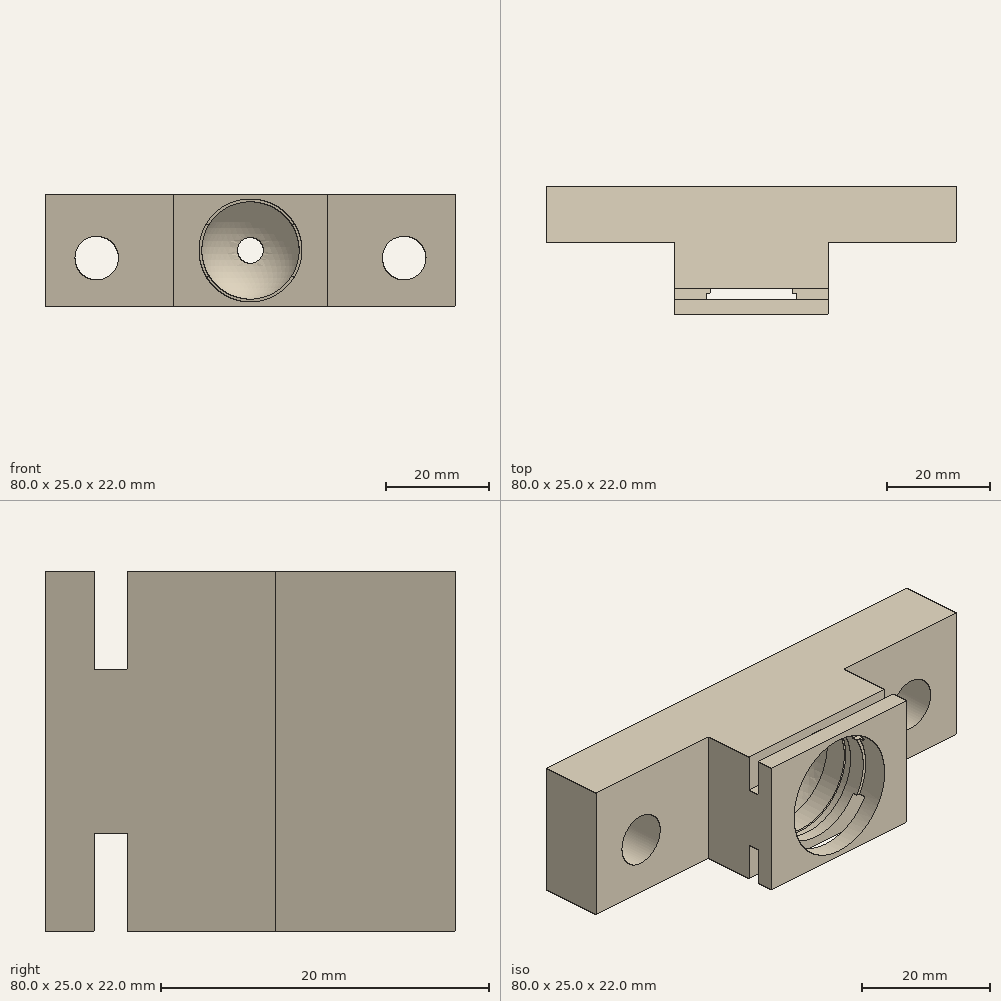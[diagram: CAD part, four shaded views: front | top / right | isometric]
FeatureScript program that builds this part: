
annotation { "Feature Type Name" : "Feature", "Feature Type Description" : "" }
export const myFeature = defineFeature(function(context is Context, id is Id, definition is map)
    precondition{}
    {
        {
            var Q0;
            Q0=qCreatedBy(makeId("Front.planeOp"),FACE);
            var sketch = newSketch(context, id + "F0", { "sketchPlane" : qUnion([Q0])});
            skLineSegment(sketch, "E0.bottom", {"start": v(40, 11) * mm, "end": v(-40, 11) * mm});
            skLineSegment(sketch, "E0.top", {"start": v(40, -11) * mm, "end": v(-40, -11) * mm});
            skLineSegment(sketch, "E0.left", {"start": v(40, 11) * mm, "end": v(40, -11) * mm});
            skLineSegment(sketch, "E0.right", {"start": v(-40, 11) * mm, "end": v(-40, -11) * mm});
            skPoint(sketch, "E0.middle", {"position": v(0, 0) * mm});
            skSolve(sketch);
        }
        {
            var Q0;
            Q0 = qSketchRegion(id + "F0", true);
            extrude(context, id + "F1", {"entities" : qUnion([Q0]), "depth" : 11 * mm, "offsetDistance" : 25 * mm});
        }
        {
            var Q0;
            Q0=makeQuery(id+"F1.opExtrude","CAP_FACE",FACE,{"disambiguationData":[OSD([sQuery(id+"F0.wireOp",EDGE,"E0.bottom"),sQuery(id+"F0.wireOp",EDGE,"E0.top"),sQuery(id+"F0.wireOp",EDGE,"E0.left"),sQuery(id+"F0.wireOp",EDGE,"E0.right")])],"isStart":false});
            var sketch = newSketch(context, id + "F2", { "sketchPlane" : qUnion([Q0])});
            skLineSegment(sketch, "E1.bottom", {"start": v(15, 11) * mm, "end": v(-15, 11) * mm});
            skLineSegment(sketch, "E1.top", {"start": v(15, -11) * mm, "end": v(-15, -11) * mm});
            skLineSegment(sketch, "E1.left", {"start": v(15, 11) * mm, "end": v(15, -11) * mm});
            skLineSegment(sketch, "E1.right", {"start": v(-15, 11) * mm, "end": v(-15, -11) * mm});
            skPoint(sketch, "E1.middle", {"position": v(0, 0) * mm});
            skSolve(sketch);
        }
        {
            var Q0;
            Q0 = qSketchRegion(id + "F2", true);
            extrude(context, id + "F3", {"entities" : qUnion([Q0]), "operationType" : NewBodyOperationType.ADD, "depth" : 14 * mm, "offsetDistance" : 25 * mm});
        }
        {
            var Q0;
            Q0=makeQuery(id+"F1.opExtrude","CAP_FACE",FACE,{"disambiguationData":[OSD([sQuery(id+"F0.wireOp",EDGE,"E0.bottom"),sQuery(id+"F0.wireOp",EDGE,"E0.top"),sQuery(id+"F0.wireOp",EDGE,"E0.left"),sQuery(id+"F0.wireOp",EDGE,"E0.right")])],"isStart":true});
            var sketch = newSketch(context, id + "F4", { "sketchPlane" : qUnion([Q0])});
            skCircle(sketch, "E2", {"center": v(30, -1.5) * mm, "radius": 4.25 * mm});
            skCircle(sketch, "E3.MirrorC", {"center": v(-30, -1.5) * mm, "radius": 4.25 * mm});
            skSolve(sketch);
        }
        {
            var Q0;
            Q0 = qSketchRegion(id + "F4", true);
            extrude(context, id + "F5", {"entities" : qUnion([Q0]), "operationType" : NewBodyOperationType.REMOVE, "endBound" : BoundingType.UP_TO_NEXT, "oppositeDirection" : true, "depth" : 25 * mm, "offsetDistance" : 25 * mm});
        }
        {
            var Q0;
            Q0=makeQuery(id+"F3.opExtrude","SWEPT_FACE",FACE,{"disambiguationData":[OSD([sQuery(id+"F2.wireOp",EDGE,"E1.right")])]});
            var sketch = newSketch(context, id + "F6", { "sketchPlane" : qUnion([Q0])});
            skLineSegment(sketch, "E4", {"start": v(22, 11) * mm, "end": v(22, 5) * mm});
            skLineSegment(sketch, "E5", {"start": v(22, 5) * mm, "end": v(20, 5) * mm});
            skLineSegment(sketch, "E6", {"start": v(20, 5) * mm, "end": v(20, 11) * mm});
            skLineSegment(sketch, "E7.MirrorCS", {"start": v(22, -11) * mm, "end": v(22, -5) * mm});
            skLineSegment(sketch, "E8.MirrorCS", {"start": v(22, -5) * mm, "end": v(20, -5) * mm});
            skLineSegment(sketch, "E9.MirrorCS", {"start": v(20, -5) * mm, "end": v(20, -11) * mm});
            skLineSegment(sketch, "E10", {"start": v(22, 11) * mm, "end": v(20, 11) * mm});
            skLineSegment(sketch, "E11", {"start": v(22, -11) * mm, "end": v(20, -11) * mm});
            skSolve(sketch);
        }
        {
            var Q0;
            Q0 = qSketchRegion(id + "F6", true);
            extrude(context, id + "F7", {"entities" : qUnion([Q0]), "operationType" : NewBodyOperationType.REMOVE, "endBound" : BoundingType.UP_TO_NEXT, "oppositeDirection" : true, "depth" : 25 * mm, "offsetDistance" : 25 * mm});
        }
        {
            var Q0;
            Q0=makeQuery(id+"F3.opExtrude","CAP_FACE",FACE,{"disambiguationData":[OSD([sQuery(id+"F2.wireOp",EDGE,"E1.bottom"),sQuery(id+"F2.wireOp",EDGE,"E1.top"),sQuery(id+"F2.wireOp",EDGE,"E1.left"),sQuery(id+"F2.wireOp",EDGE,"E1.right")])],"isStart":false});
            var sketch = newSketch(context, id + "F8", { "sketchPlane" : qUnion([Q0])});
            skCircle(sketch, "E12", {"center": v(0, 0) * mm, "radius": 10.05 * mm});
            skSolve(sketch);
        }
        {
            var Q0;
            Q0 = qSketchRegion(id + "F8", true);
            extrude(context, id + "F9", {"entities" : qUnion([Q0]), "operationType" : NewBodyOperationType.REMOVE, "oppositeDirection" : true, "depth" : 4.2 * mm, "offsetDistance" : 25 * mm});
        }
        {
            var Q0;
            Q0=makeQuery(id+"F3.opExtrude","CAP_FACE",FACE,{"disambiguationData":[OSD([sQuery(id+"F2.wireOp",EDGE,"E1.bottom"),sQuery(id+"F2.wireOp",EDGE,"E1.top"),sQuery(id+"F2.wireOp",EDGE,"E1.left"),sQuery(id+"F2.wireOp",EDGE,"E1.right")])],"isStart":false});
            var sketch = newSketch(context, id + "F10", { "sketchPlane" : qUnion([Q0])});
            skCircle(sketch, "E13", {"center": v(0, 0) * mm, "radius": 9.5 * mm});
            skSolve(sketch);
        }
        {
            var Q0;
            Q0 = qSketchRegion(id + "F10", true);
            extrude(context, id + "F11", {"entities" : qUnion([Q0]), "operationType" : NewBodyOperationType.REMOVE, "oppositeDirection" : true, "depth" : 7 * mm, "offsetDistance" : 25 * mm});
        }
        {
            var Q0;
            Q0=makeQuery(id+"F3.opExtrude","CAP_FACE",FACE,{"disambiguationData":[OSD([sQuery(id+"F2.wireOp",EDGE,"E1.bottom"),sQuery(id+"F2.wireOp",EDGE,"E1.top"),sQuery(id+"F2.wireOp",EDGE,"E1.left"),sQuery(id+"F2.wireOp",EDGE,"E1.right")])],"isStart":false});
            var sketch = newSketch(context, id + "F12", { "sketchPlane" : qUnion([Q0])});
            skCircle(sketch, "E14", {"center": v(0, 0) * mm, "radius": 9.8 * mm});
            skSolve(sketch);
        }
        {
            var Q0;
            Q0=makeQuery(id+"F12.imprint","IMPRINT",FACE,{"disambiguationData":[TD([[makeQuery(id+"F12.imprint","IMPRINT",EDGE,{"derivedFrom":sQuery(id+"F12.wireOp",EDGE,"E14")}),-1.0]])]});
            cPlane(context, id + "F13", {"entities" : qUnion([Q0]), "cplaneType" : CPlaneType.OFFSET, "offset" : 7 * mm, "oppositeDirection" : true, "width" : 150 * mm, "height" : 150 * mm});
        }
        {
            var Q0;
            Q0=qCreatedBy(id+"F13.planeOp",FACE);
            var sketch = newSketch(context, id + "F14", { "sketchPlane" : qUnion([Q0])});
            skCircle(sketch, "E15", {"center": v(0, 0) * mm, "radius": 9.8 * mm});
            skSolve(sketch);
        }
        {
            var Q0;
            Q0 = qSketchRegion(id + "F14", true);
            extrude(context, id + "F15", {"entities" : qUnion([Q0]), "operationType" : NewBodyOperationType.REMOVE, "oppositeDirection" : true, "depth" : 1.4 * mm, "offsetDistance" : 25 * mm});
        }
        {
            var Q0;
            Q0=makeQuery(id+"F12.imprint","IMPRINT",FACE,{"disambiguationData":[TD([[makeQuery(id+"F12.imprint","IMPRINT",EDGE,{"derivedFrom":sQuery(id+"F12.wireOp",EDGE,"E14")}),-1.0]])]});
            cPlane(context, id + "F16", {"entities" : qUnion([Q0]), "cplaneType" : CPlaneType.OFFSET, "offset" : 8.4 * mm, "oppositeDirection" : true, "width" : 150 * mm, "height" : 150 * mm});
        }
        {
            var Q0;
            Q0=qCreatedBy(id+"F16.planeOp",FACE);
            var sketch = newSketch(context, id + "F17", { "sketchPlane" : qUnion([Q0])});
            skCircle(sketch, "E16", {"center": v(0, 0) * mm, "radius": 9.5 * mm});
            skSolve(sketch);
        }
        {
            var Q0;
            Q0 = qSketchRegion(id + "F17", true);
            extrude(context, id + "F18", {"entities" : qUnion([Q0]), "operationType" : NewBodyOperationType.REMOVE, "oppositeDirection" : true, "depth" : 3.8 * mm, "offsetDistance" : 25 * mm});
        }
        {
            var Q0;
            Q0=makeQuery(id+"F1.opExtrude","CAP_FACE",FACE,{"disambiguationData":[OSD([sQuery(id+"F0.wireOp",EDGE,"E0.bottom"),sQuery(id+"F0.wireOp",EDGE,"E0.top"),sQuery(id+"F0.wireOp",EDGE,"E0.left"),sQuery(id+"F0.wireOp",EDGE,"E0.right")])],"isStart":true});
            var sketch = newSketch(context, id + "F19", { "sketchPlane" : qUnion([Q0])});
            skCircle(sketch, "E17", {"center": v(0, 0) * mm, "radius": 2.5 * mm});
            skSolve(sketch);
        }
        {
            var Q0;
            Q0=qCreatedBy(id+"F16.planeOp",FACE);
            var sketch = newSketch(context, id + "F20", { "sketchPlane" : qUnion([Q0])});
            skCircle(sketch, "E18", {"center": v(0, 0) * mm, "radius": 9.5 * mm});
            skSolve(sketch);
        }
        {
            var Q0;
            Q0 = qSketchRegion(id + "F20", true);
            extrude(context, id + "F21", {"entities" : qUnion([Q0]), "operationType" : NewBodyOperationType.REMOVE, "oppositeDirection" : true, "depth" : 3.8 * mm, "offsetDistance" : 25 * mm});
        }
        {
            var Q0;
            Q0 = qSketchRegion(id + "F19", true);
            extrude(context, id + "F22", {"entities" : qUnion([Q0]), "operationType" : NewBodyOperationType.REMOVE, "oppositeDirection" : true, "depth" : 3.8 * mm, "offsetDistance" : 25 * mm});
        }
        {
            var Q0;
            Q0=qCreatedBy(makeId("Right.planeOp"),FACE);
            var sketch = newSketch(context, id + "F23", { "sketchPlane" : qUnion([Q0])});
            skArc(sketch, "E19", {"start": v(-12.91, -9.5) * mm, "mid": v(-3.41, 0) * mm, "end": v(-12.91, 9.5) * mm});
            skLineSegment(sketch, "E20", {"start": v(-12.91, -9.5) * mm, "end": v(-12.91, 9.5) * mm});
            skSolve(sketch);
        }
        {
            var Q0;
            Q0 = qSketchRegion(id + "F23", true);
            var Q1;
            Q1=sQuery(id+"F23.wireOp",EDGE,"E20");
            revolve(context, id + "F24", {"operationType" : NewBodyOperationType.REMOVE, "entities" : qUnion([Q0]), "axis" : qUnion([Q1]), "revolveType" : RevolveType.FULL, "oppositeDirection" : true});
        }
    });
